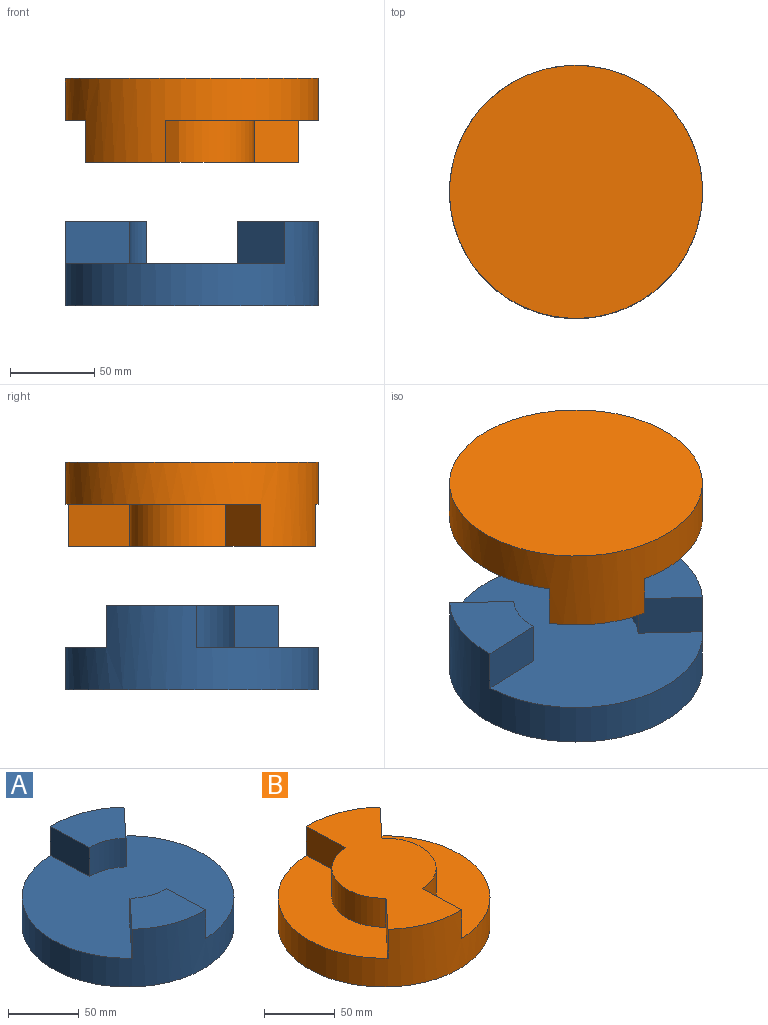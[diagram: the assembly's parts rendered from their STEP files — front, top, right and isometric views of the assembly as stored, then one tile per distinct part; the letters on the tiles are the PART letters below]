
ASSEMBLY  parts=2 mates=1
PART A: 11 faces, bbox 150x150x50 mm
  f0: plane 38.05x25mm, normal (-1,-0.04,0), area 952mm2, adj f2,f3,f4,f5
  f1: plane 27.93x25.89mm, normal (0.73,-0.68,0), area 952mm2, adj f2,f3,f4,f5
  f2: cylinder r=75.02mm len=150.04mm, axis (0,0,-1), area 14730.6mm2, adj f0,f1,f3,f5,f6,f7,f8,f9
  f3: plane 53.84x47.93mm, normal (0,0,1), area 1674.3mm2, adj f0,f1,f2,f4
  f4: cylinder r=36.94mm len=26.51mm, axis (0,0,-1), area 725.4mm2, adj f0,f1,f3,f5
  f5: plane 150.04x149.94mm, normal (0,0,1), area 14333.4mm2, adj f0,f1,f2,f4,f7,f8,f10
  f6: plane 150.04x150.04mm, normal (0,0,-1), area 17682mm2, adj f2
  f7: plane 38.05x25mm, normal (1,0.04,0), area 952mm2, adj f2,f5,f9,f10
  f8: plane 27.93x25.89mm, normal (-0.73,0.68,0), area 952mm2, adj f2,f5,f9,f10
  f9: plane 53.84x47.93mm, normal (0,0,1), area 1674.3mm2, adj f2,f7,f8,f10
  f10: cylinder r=36.94mm len=26.51mm, axis (0,0,-1), area 725.4mm2, adj f5,f7,f8,f9
PART B: 11 faces, bbox 150x150x50 mm
  f0: plane 38.05x25mm, normal (1,0.04,0), area 952mm2, adj f2,f3,f4,f10
  f1: plane 27.93x25.89mm, normal (-0.73,0.68,0), area 952mm2, adj f2,f3,f5,f9
  f2: cylinder r=75.02mm len=150.04mm, axis (0,0,-1), area 14730.6mm2, adj f0,f1,f3,f4,f6,f7,f8,f9
  f3: plane 150.04x101.99mm, normal (0,0,1), area 7636.1mm2, adj f0,f1,f2,f5,f6,f7,f10
  f4: plane 129.99x73.62mm, normal (0,0,1), area 5022.9mm2, adj f0,f2,f7,f10
  f5: cylinder r=36.94mm len=64.01mm, axis (0,0,-1), area 2176.1mm2, adj f1,f3,f6,f9
  f6: plane 38.05x25mm, normal (-1,-0.04,0), area 952mm2, adj f2,f3,f5,f9
  f7: plane 27.93x25.89mm, normal (0.73,-0.68,0), area 952mm2, adj f2,f3,f4,f10
  f8: plane 150.04x150.04mm, normal (0,0,-1), area 17682mm2, adj f2
  f9: plane 129.99x73.62mm, normal (0,0,1), area 5022.9mm2, adj f1,f2,f5,f6
  f10: cylinder r=36.94mm len=64.01mm, axis (0,0,-1), area 2176.1mm2, adj f0,f3,f4,f7
PLACE A rot(axis=(0,0,1),90deg) t=(161.33,-148.07,2.65)mm
PLACE B rot(axis=(-0.46,-0.89,0),180deg) t=(161.33,-148.07,87.65)mm
MATE fastened B.f2 <-> A.f4  axis (0,0,-1) through (161.33,-148.07,62.65)mm
